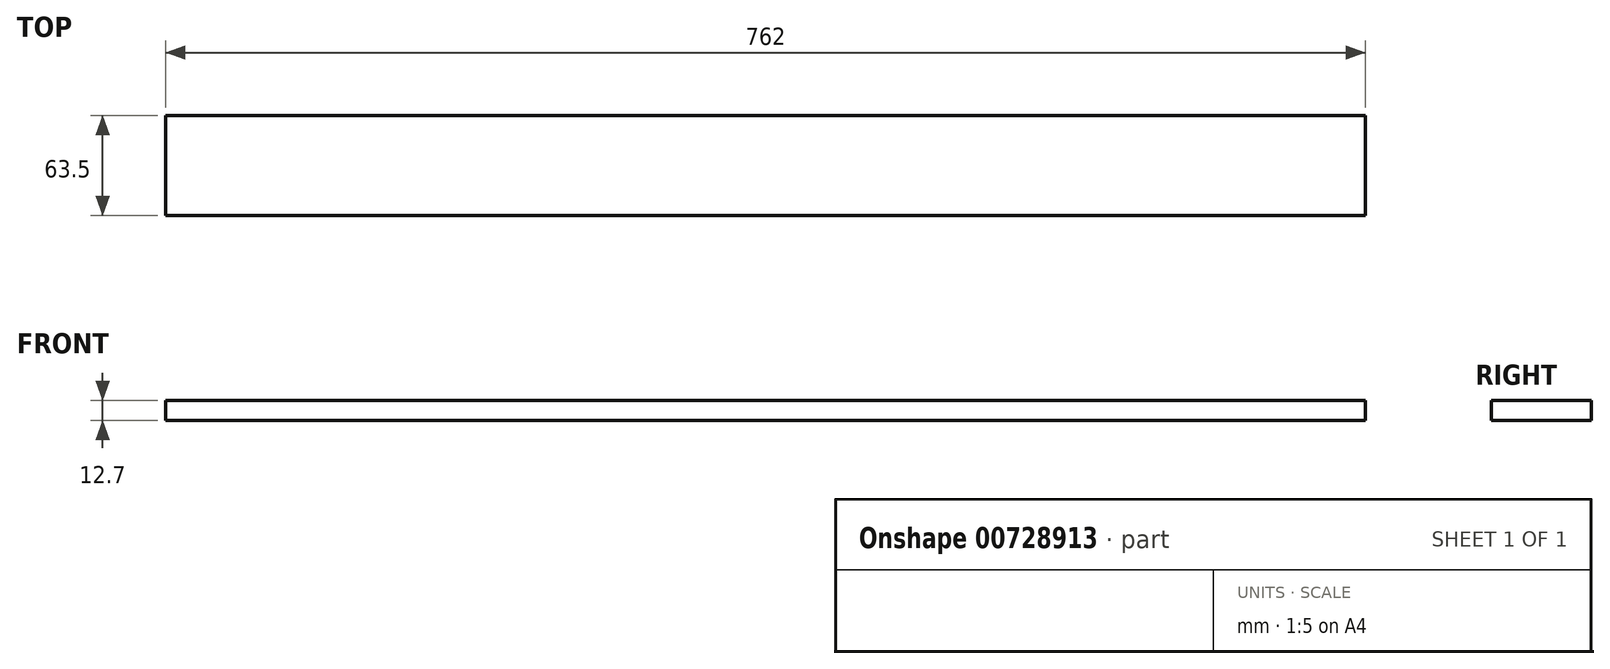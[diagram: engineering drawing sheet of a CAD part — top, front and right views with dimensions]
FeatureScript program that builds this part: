
annotation { "Feature Type Name" : "Feature", "Feature Type Description" : "" }
export const myFeature = defineFeature(function(context is Context, id is Id, definition is map)
    precondition{}
    {
        {
            var Q0;
            Q0=qCreatedBy(makeId("Top.planeOp"),FACE);
            var sketch = newSketch(context, id + "F0", { "sketchPlane" : qUnion([Q0])});
            skLineSegment(sketch, "E0.bottom", {"start": v(381, -31.75) * mm, "end": v(-381, -31.75) * mm});
            skLineSegment(sketch, "E0.top", {"start": v(381, 31.75) * mm, "end": v(-381, 31.75) * mm});
            skLineSegment(sketch, "E0.left", {"start": v(381, -31.75) * mm, "end": v(381, 31.75) * mm});
            skLineSegment(sketch, "E0.right", {"start": v(-381, -31.75) * mm, "end": v(-381, 31.75) * mm});
            skPoint(sketch, "E0.middle", {"position": v(0, 0) * mm});
            skSolve(sketch);
        }
        {
            var Q0;
            Q0=makeQuery(id+"F0.imprint","IMPRINT",FACE,{"disambiguationData":[TD([[makeQuery(id+"F0.imprint","IMPRINT",EDGE,{"derivedFrom":sQuery(id+"F0.wireOp",EDGE,"E0.bottom")}),-1.0]])]});
            extrude(context, id + "F1", {"entities" : qUnion([Q0]), "oppositeDirection" : true, "depth" : 12.7 * mm, "offsetDistance" : 25.4 * mm});
        }
    });
